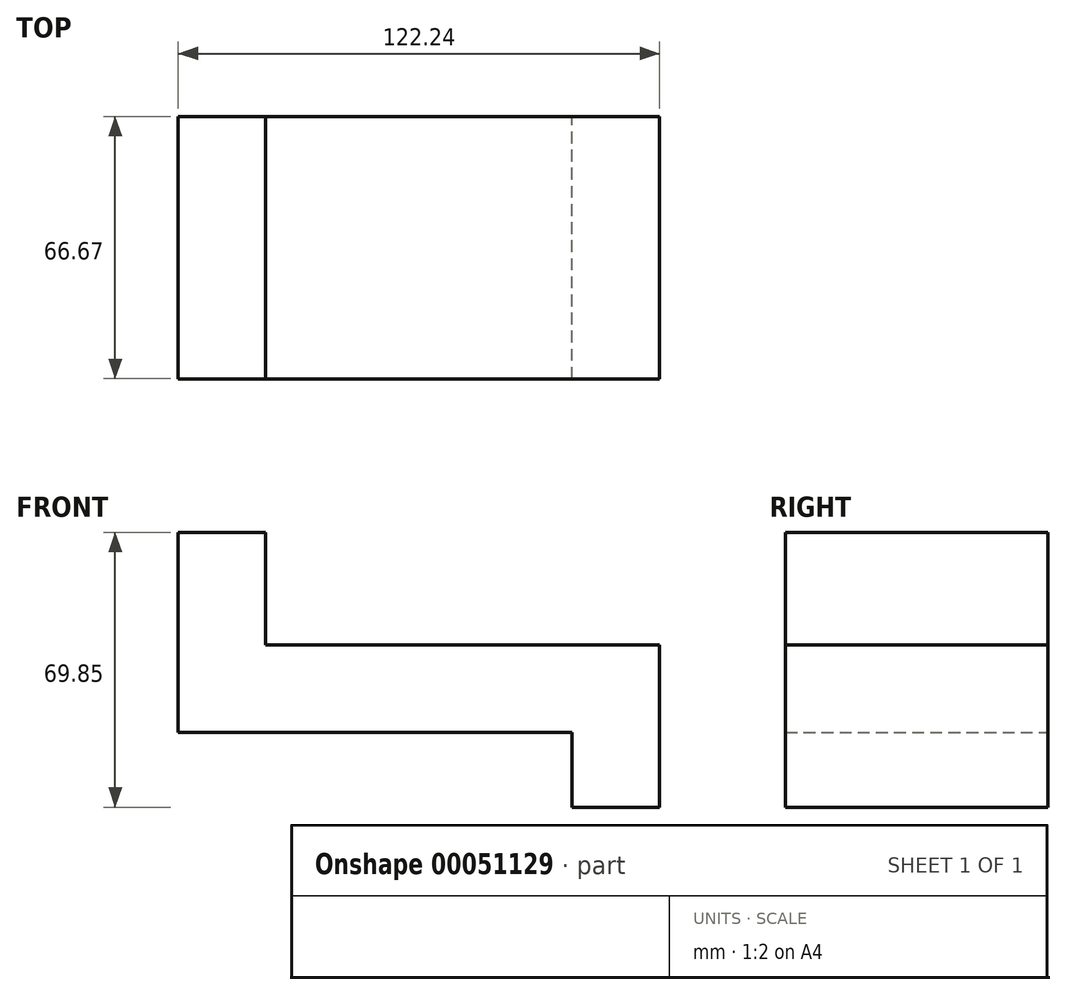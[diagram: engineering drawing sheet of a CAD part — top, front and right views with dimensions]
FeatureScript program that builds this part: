
annotation { "Feature Type Name" : "Feature", "Feature Type Description" : "" }
export const myFeature = defineFeature(function(context is Context, id is Id, definition is map)
    precondition{}
    {
        {
            var Q0;
            Q0=qCreatedBy(makeId("Front.planeOp"),FACE);
            var sketch = newSketch(context, id + "F0", { "sketchPlane" : qUnion([Q0])});
            skLineSegment(sketch, "E0", {"start": v(-74.22, 0) * mm, "end": v(25.8, 0) * mm});
            skLineSegment(sketch, "E1", {"start": v(-74.22, 0) * mm, "end": v(-74.22, 50.8) * mm});
            skLineSegment(sketch, "E2", {"start": v(-74.22, 50.8) * mm, "end": v(-52, 50.8) * mm});
            skLineSegment(sketch, "E3", {"start": v(-52, 50.8) * mm, "end": v(-52, 22.22) * mm});
            skLineSegment(sketch, "E4", {"start": v(-52, 22.22) * mm, "end": v(48.02, 22.23) * mm});
            skLineSegment(sketch, "E5", {"start": v(48.02, -19.05) * mm, "end": v(25.8, -19.05) * mm});
            skLineSegment(sketch, "E6", {"start": v(25.8, -19.05) * mm, "end": v(25.8, 0) * mm});
            skPoint(sketch, "E7.start.orphan", {"position": v(48.02, 0) * mm});
            skLineSegment(sketch, "E8", {"start": v(48.02, 22.23) * mm, "end": v(48.02, -19.05) * mm});
            skSolve(sketch);
        }
        {
            var Q0;
            Q0 = qSketchRegion(id + "F0", true);
            extrude(context, id + "F1", {"entities" : qUnion([Q0]), "depth" : 66.67 * mm});
        }
    });
